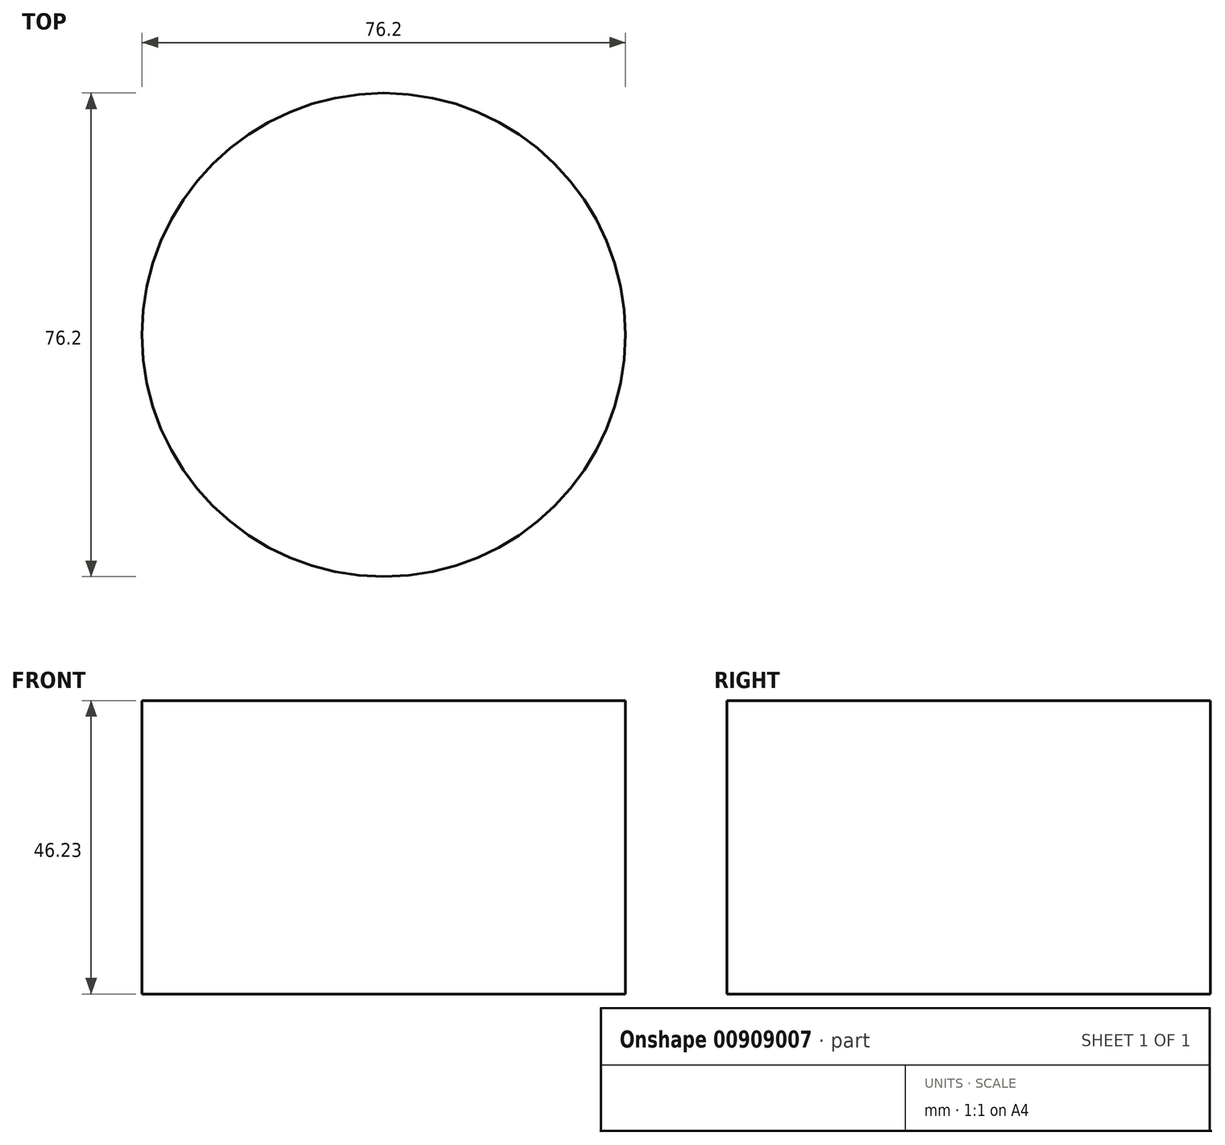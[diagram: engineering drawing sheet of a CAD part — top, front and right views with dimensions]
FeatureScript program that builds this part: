
annotation { "Feature Type Name" : "Feature", "Feature Type Description" : "" }
export const myFeature = defineFeature(function(context is Context, id is Id, definition is map)
    precondition{}
    {
        {
            var Q0;
            Q0=qCreatedBy(makeId("Top.planeOp"),FACE);
            var sketch = newSketch(context, id + "F0", { "sketchPlane" : qUnion([Q0])});
            skCircle(sketch, "E0", {"center": v(0, 0) * mm, "radius": 38.1 * mm});
            skSolve(sketch);
        }
        {
            var Q0;
            Q0=makeQuery(id+"F0.imprint","IMPRINT",FACE,{"disambiguationData":[TD([[makeQuery(id+"F0.imprint","IMPRINT",EDGE,{"derivedFrom":sQuery(id+"F0.wireOp",EDGE,"E0")}),1.0]])]});
            extrude(context, id + "F1", {"entities" : qUnion([Q0]), "depth" : 46.23 * mm, "offsetDistance" : 25.4 * mm});
        }
    });
